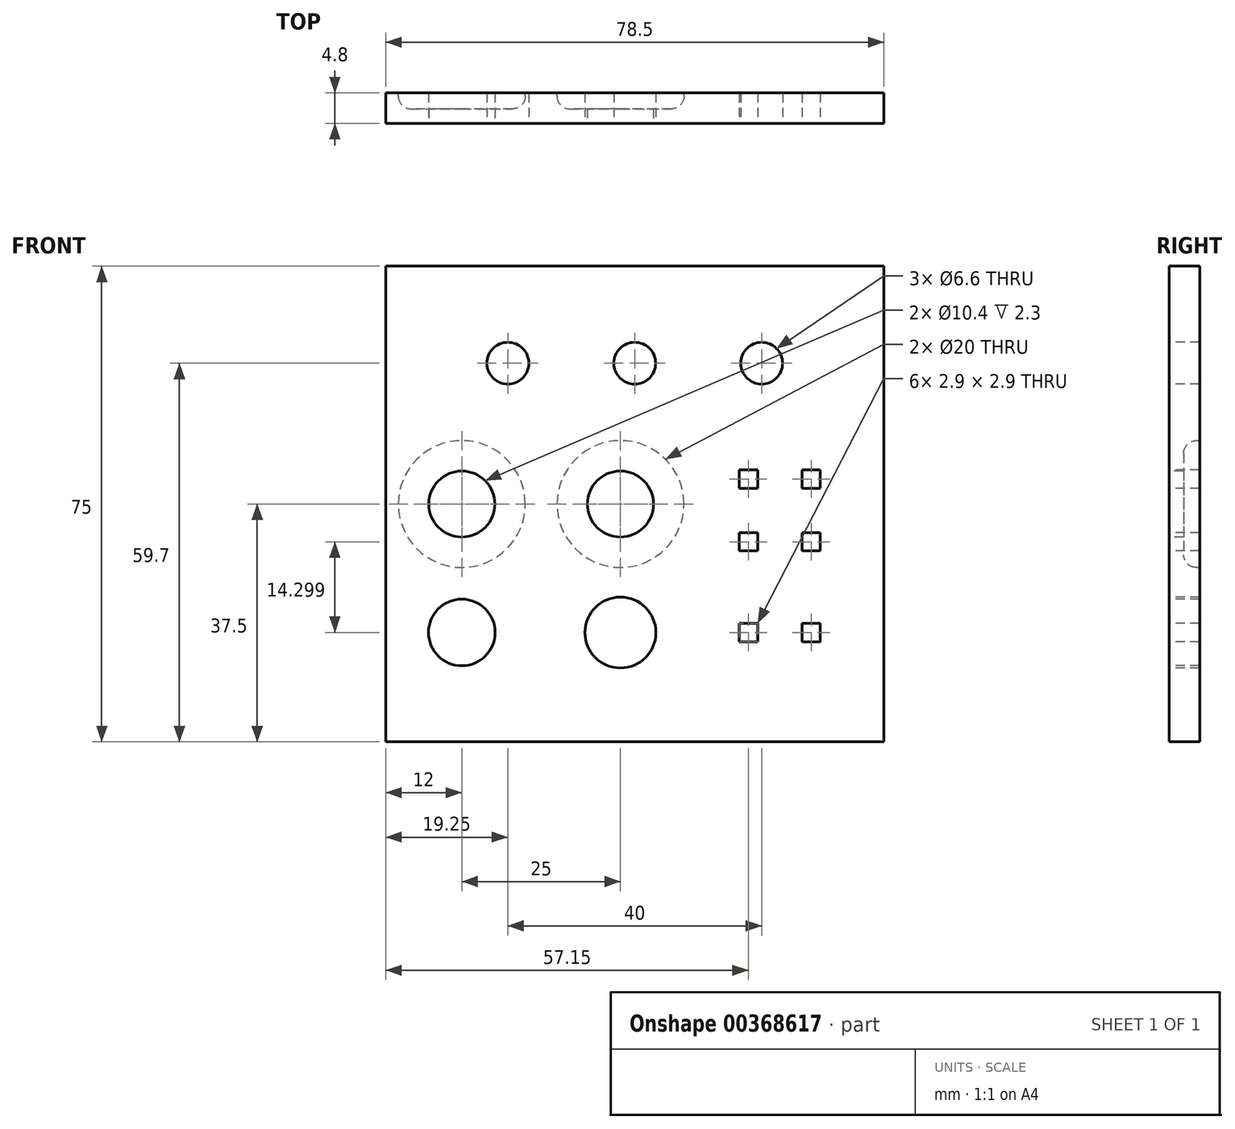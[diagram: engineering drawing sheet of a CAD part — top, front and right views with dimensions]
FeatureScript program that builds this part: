
annotation { "Feature Type Name" : "Feature", "Feature Type Description" : "" }
export const myFeature = defineFeature(function(context is Context, id is Id, definition is map)
    precondition{}
    {
        {
            var Q0;
            Q0=qCreatedBy(makeId("Front.planeOp"),FACE);
            var sketch = newSketch(context, id + "F0", { "sketchPlane" : qUnion([Q0])});
            skLineSegment(sketch, "E0.bottom", {"start": v(39.25, -37.5) * mm, "end": v(-39.25, -37.5) * mm});
            skLineSegment(sketch, "E0.top", {"start": v(39.25, 37.5) * mm, "end": v(-39.25, 37.5) * mm});
            skLineSegment(sketch, "E0.left", {"start": v(39.25, -37.5) * mm, "end": v(39.25, 37.5) * mm});
            skLineSegment(sketch, "E0.right", {"start": v(-39.25, -37.5) * mm, "end": v(-39.25, 37.5) * mm});
            skPoint(sketch, "E0.middle", {"position": v(0, 0) * mm});
            skSolve(sketch);
        }
        {
            var Q0;
            Q0=qSketchRegion(id+"F0",true);
            extrude(context, id + "F1", {"entities" : qUnion([Q0]), "depth" : 4.8 * mm});
        }
        {
            var Q0;
            Q0=makeQuery(id+"F1.opExtrude","CAP_FACE",FACE,{"disambiguationData":[OSD([sQuery(id+"F0.wireOp",EDGE,"E0.bottom"),sQuery(id+"F0.wireOp",EDGE,"E0.top"),sQuery(id+"F0.wireOp",EDGE,"E0.left"),sQuery(id+"F0.wireOp",EDGE,"E0.right")])],"isStart":false});
            var sketch = newSketch(context, id + "F2", { "sketchPlane" : qUnion([Q0])});
            skCircle(sketch, "E1", {"center": v(-27.25, 0) * mm, "radius": 5.2 * mm});
            skCircle(sketch, "E2", {"center": v(-27.25, -20.25) * mm, "radius": 5.25 * mm});
            skCircle(sketch, "E3", {"center": v(-2.25, -20.25) * mm, "radius": 5.6 * mm});
            skCircle(sketch, "E4", {"center": v(-2.25, 0) * mm, "radius": 5.2 * mm});
            skCircle(sketch, "E5", {"center": v(0, 22.2) * mm, "radius": 3.3 * mm});
            skCircle(sketch, "E6", {"center": v(-20, 22.2) * mm, "radius": 3.3 * mm});
            skCircle(sketch, "E7", {"center": v(20, 22.2) * mm, "radius": 3.3 * mm});
            skLineSegment(sketch, "E8.bottom", {"start": v(19.35, 2.5) * mm, "end": v(16.45, 2.5) * mm});
            skLineSegment(sketch, "E8.top", {"start": v(19.35, 5.4) * mm, "end": v(16.45, 5.4) * mm});
            skLineSegment(sketch, "E8.left", {"start": v(19.35, 2.5) * mm, "end": v(19.35, 5.4) * mm});
            skLineSegment(sketch, "E8.right", {"start": v(16.45, 2.5) * mm, "end": v(16.45, 5.4) * mm});
            skPoint(sketch, "E8.middle", {"position": v(17.9, 3.95) * mm});
            skLineSegment(sketch, "E9.bottom", {"start": v(26.35, 5.4) * mm, "end": v(29.25, 5.4) * mm});
            skLineSegment(sketch, "E9.top", {"start": v(26.35, 2.5) * mm, "end": v(29.25, 2.5) * mm});
            skLineSegment(sketch, "E9.left", {"start": v(26.35, 5.4) * mm, "end": v(26.35, 2.5) * mm});
            skLineSegment(sketch, "E9.right", {"start": v(29.25, 5.4) * mm, "end": v(29.25, 2.5) * mm});
            skPoint(sketch, "E9.middle", {"position": v(27.8, 3.95) * mm});
            skLineSegment(sketch, "E10.bottom", {"start": v(19.35, -7.4) * mm, "end": v(16.45, -7.4) * mm});
            skLineSegment(sketch, "E10.top", {"start": v(19.35, -4.5) * mm, "end": v(16.45, -4.5) * mm});
            skLineSegment(sketch, "E10.left", {"start": v(19.35, -7.4) * mm, "end": v(19.35, -4.5) * mm});
            skLineSegment(sketch, "E10.right", {"start": v(16.45, -7.4) * mm, "end": v(16.45, -4.5) * mm});
            skPoint(sketch, "E10.middle", {"position": v(17.9, -5.95) * mm});
            skLineSegment(sketch, "E11.bottom", {"start": v(29.25, -7.4) * mm, "end": v(26.35, -7.4) * mm});
            skLineSegment(sketch, "E11.top", {"start": v(29.25, -4.5) * mm, "end": v(26.35, -4.5) * mm});
            skLineSegment(sketch, "E11.left", {"start": v(29.25, -7.4) * mm, "end": v(29.25, -4.5) * mm});
            skLineSegment(sketch, "E11.right", {"start": v(26.35, -7.4) * mm, "end": v(26.35, -4.5) * mm});
            skPoint(sketch, "E11.middle", {"position": v(27.8, -5.95) * mm});
            skLineSegment(sketch, "E12.bottom", {"start": v(19.35, -21.7) * mm, "end": v(16.45, -21.7) * mm});
            skLineSegment(sketch, "E12.top", {"start": v(19.35, -18.8) * mm, "end": v(16.45, -18.8) * mm});
            skLineSegment(sketch, "E12.left", {"start": v(19.35, -21.7) * mm, "end": v(19.35, -18.8) * mm});
            skLineSegment(sketch, "E12.right", {"start": v(16.45, -21.7) * mm, "end": v(16.45, -18.8) * mm});
            skPoint(sketch, "E12.middle", {"position": v(17.9, -20.25) * mm});
            skPoint(sketch, "E13.middle.positionSnap0", {"position": v(19.35, -20.25) * mm});
            skPoint(sketch, "E13.centerSnap0", {"position": v(19.35, -20.25) * mm});
            skLineSegment(sketch, "E14.bottom", {"start": v(26.35, -21.7) * mm, "end": v(29.25, -21.7) * mm});
            skLineSegment(sketch, "E14.top", {"start": v(26.35, -18.8) * mm, "end": v(29.25, -18.8) * mm});
            skLineSegment(sketch, "E14.left", {"start": v(26.35, -21.7) * mm, "end": v(26.35, -18.8) * mm});
            skLineSegment(sketch, "E14.right", {"start": v(29.25, -21.7) * mm, "end": v(29.25, -18.8) * mm});
            skPoint(sketch, "E14.middle", {"position": v(27.8, -20.25) * mm});
            skSolve(sketch);
        }
        {
            var Q0;
            Q0=qSketchRegion(id+"F2",true);
            extrude(context, id + "F3", {"entities" : qUnion([Q0]), "operationType" : NewBodyOperationType.REMOVE, "endBound" : BoundingType.THROUGH_ALL, "oppositeDirection" : true, "depth" : 25 * mm});
        }
        {
            var Q0;
            Q0=makeQuery(id+"F1.opExtrude","CAP_FACE",FACE,{"disambiguationData":[OSD([sQuery(id+"F0.wireOp",EDGE,"E0.bottom"),sQuery(id+"F0.wireOp",EDGE,"E0.top"),sQuery(id+"F0.wireOp",EDGE,"E0.left"),sQuery(id+"F0.wireOp",EDGE,"E0.right")])],"isStart":true});
            var sketch = newSketch(context, id + "F4", { "sketchPlane" : qUnion([Q0])});
            skCircle(sketch, "E15", {"center": v(2.25, 0) * mm, "radius": 10 * mm});
            skCircle(sketch, "E16", {"center": v(27.25, 0) * mm, "radius": 10 * mm});
            skSolve(sketch);
        }
        {
            var Q0;
            Q0=qSketchRegion(id+"F4",true);
            extrude(context, id + "F5", {"entities" : qUnion([Q0]), "operationType" : NewBodyOperationType.REMOVE, "oppositeDirection" : true, "depth" : 2.5 * mm});
        }
        {
            var Q0;
            Q0=makeQuery(id+"F5.boolean.opBoolean","COPY",EDGE,{"derivedFrom":makeQuery(id+"F5.opExtrude","CAP_EDGE",EDGE,{"disambiguationData":[OSD([sQuery(id+"F4.wireOp",EDGE,"E15")])],"isStart":false})});
            var Q1;
            Q1=makeQuery(id+"F5.boolean.opBoolean","COPY",EDGE,{"derivedFrom":makeQuery(id+"F5.opExtrude","CAP_EDGE",EDGE,{"disambiguationData":[OSD([sQuery(id+"F4.wireOp",EDGE,"E16")])],"isStart":false})});
            fillet(context, id + "F6", {"entities" : qUnion([Q0, Q1]), "radius" : 2 * mm, "tangentPropagation" : true, "allowEdgeOverflow" : false});
        }
    });
